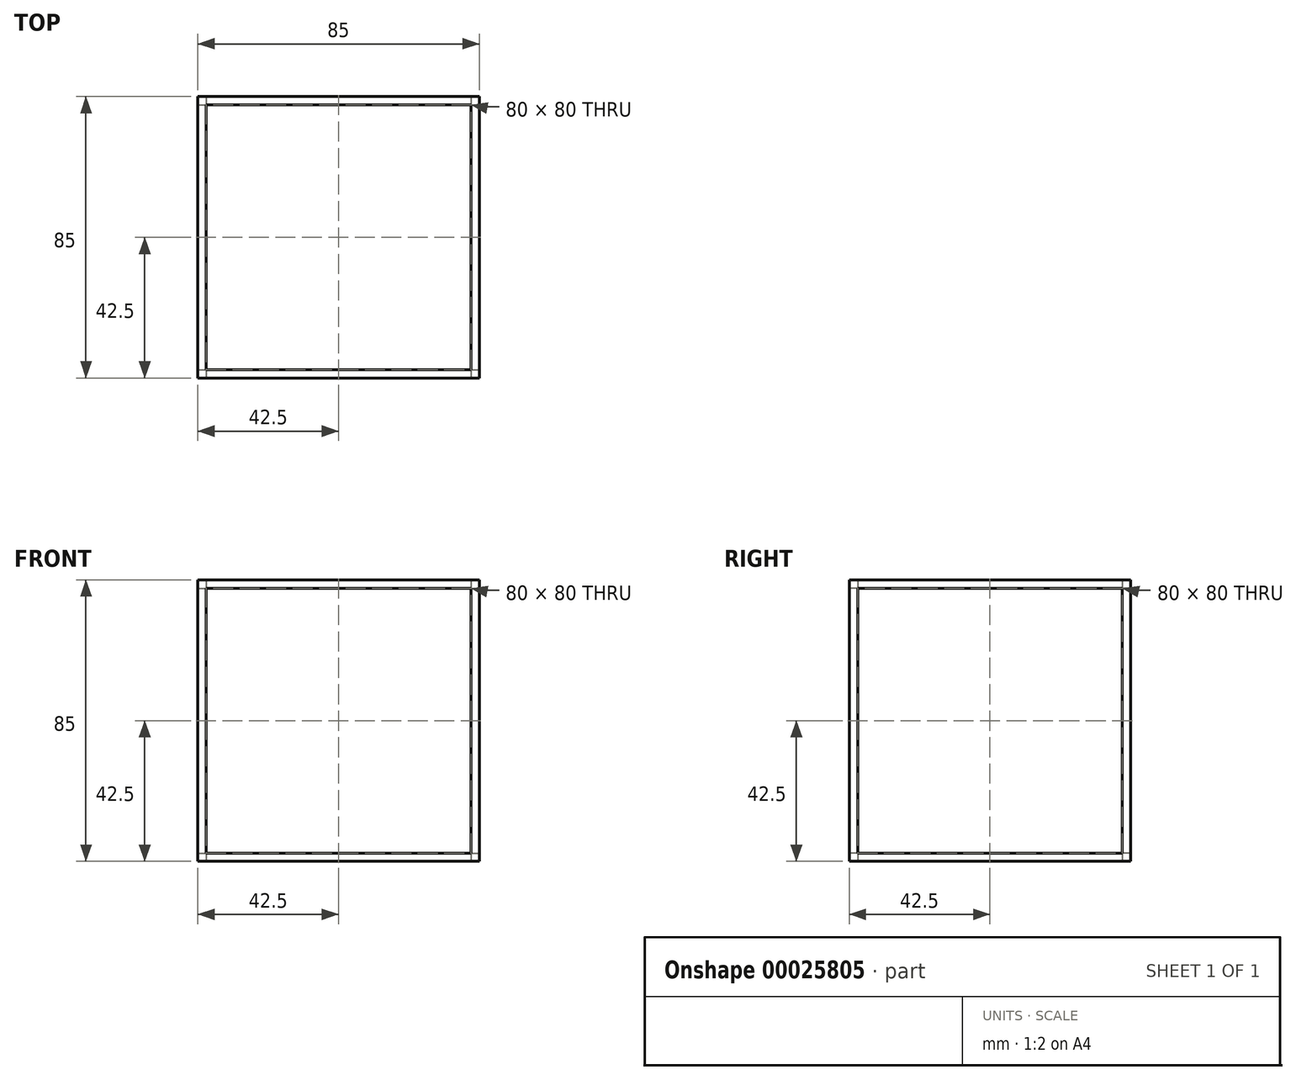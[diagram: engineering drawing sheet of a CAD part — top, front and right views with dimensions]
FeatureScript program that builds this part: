
annotation { "Feature Type Name" : "Feature", "Feature Type Description" : "" }
export const myFeature = defineFeature(function(context is Context, id is Id, definition is map)
    precondition{}
    {
        {
            var Q0;
            Q0=qCreatedBy(makeId("Top.planeOp"),FACE);
            var sketch = newSketch(context, id + "F0", { "sketchPlane" : qUnion([Q0])});
            skLineSegment(sketch, "E0.rect.bottom", {"start": v(-42.5, 42.5) * mm, "end": v(42.5, 42.5) * mm});
            skLineSegment(sketch, "E0.rect.top", {"start": v(-42.5, -42.5) * mm, "end": v(42.5, -42.5) * mm});
            skLineSegment(sketch, "E0.rect.left", {"start": v(-42.5, 42.5) * mm, "end": v(-42.5, -42.5) * mm});
            skLineSegment(sketch, "E0.rect.right", {"start": v(42.5, 42.5) * mm, "end": v(42.5, -42.5) * mm});
            skPoint(sketch, "E0.rect.middle", {"position": v(0, 0) * mm});
            skLineSegment(sketch, "E1.rect.bottom", {"start": v(-40, 40) * mm, "end": v(40, 40) * mm});
            skLineSegment(sketch, "E1.rect.top", {"start": v(-40, -40) * mm, "end": v(40, -40) * mm});
            skLineSegment(sketch, "E1.rect.left", {"start": v(-40, 40) * mm, "end": v(-40, -40) * mm});
            skLineSegment(sketch, "E1.rect.right", {"start": v(40, 40) * mm, "end": v(40, -40) * mm});
            skSolve(sketch);
        }
        {
            var Q0;
            Q0=makeQuery(id+"F0.imprint","IMPRINT",FACE,{"disambiguationData":[TD([[makeQuery(id+"F0.imprint","IMPRINT",EDGE,{"derivedFrom":sQuery(id+"F0.wireOp",EDGE,"E0.rect.bottom")}),-1.0]])]});
            extrude(context, id + "F1", {"entities" : qUnion([Q0]), "depth" : 42.5 * mm, "hasSecondDirection" : true, "secondDirectionOppositeDirection" : true, "secondDirectionDepth" : 42.5 * mm});
        }
        {
            var Q0;
            Q0=qCreatedBy(makeId("Right.planeOp"),FACE);
            var sketch = newSketch(context, id + "F2", { "sketchPlane" : qUnion([Q0])});
            skLineSegment(sketch, "E2.rect.bottom", {"start": v(-42.5, 42.5) * mm, "end": v(42.5, 42.5) * mm});
            skLineSegment(sketch, "E2.rect.top", {"start": v(-42.5, -42.5) * mm, "end": v(42.5, -42.5) * mm});
            skLineSegment(sketch, "E2.rect.left", {"start": v(-42.5, 42.5) * mm, "end": v(-42.5, -42.5) * mm});
            skLineSegment(sketch, "E2.rect.right", {"start": v(42.5, 42.5) * mm, "end": v(42.5, -42.5) * mm});
            skPoint(sketch, "E2.rect.middle", {"position": v(0, 0) * mm});
            skLineSegment(sketch, "E3.rect.bottom", {"start": v(-40, 40) * mm, "end": v(40, 40) * mm});
            skLineSegment(sketch, "E3.rect.top", {"start": v(-40, -40) * mm, "end": v(40, -40) * mm});
            skLineSegment(sketch, "E3.rect.left", {"start": v(-40, 40) * mm, "end": v(-40, -40) * mm});
            skLineSegment(sketch, "E3.rect.right", {"start": v(40, 40) * mm, "end": v(40, -40) * mm});
            skLineSegment(sketch, "E4.top", {"start": v(-40, -36) * mm, "end": v(40, -36) * mm});
            skLineSegment(sketch, "E4.left", {"start": v(-40, -40) * mm, "end": v(-40, -36) * mm});
            skLineSegment(sketch, "E4.right", {"start": v(40, -40) * mm, "end": v(40, -36) * mm});
            skLineSegment(sketch, "E5.bottom", {"start": v(-40, -26) * mm, "end": v(40, -26) * mm});
            skLineSegment(sketch, "E5.top", {"start": v(-40, -35) * mm, "end": v(40, -35) * mm});
            skLineSegment(sketch, "E5.left", {"start": v(-40, -26) * mm, "end": v(-40, -35) * mm});
            skLineSegment(sketch, "E5.right", {"start": v(40, -26) * mm, "end": v(40, -35) * mm});
            skLineSegment(sketch, "E6.bottom", {"start": v(-40, -25) * mm, "end": v(40, -25) * mm});
            skLineSegment(sketch, "E6.top", {"start": v(-40, -16) * mm, "end": v(40, -16) * mm});
            skLineSegment(sketch, "E6.left", {"start": v(-40, -25) * mm, "end": v(-40, -16) * mm});
            skLineSegment(sketch, "E6.right", {"start": v(40, -25) * mm, "end": v(40, -16) * mm});
            skSolve(sketch);
        }
        {
            var Q0;
            Q0=makeQuery(id+"F2.imprint","IMPRINT",FACE,{"disambiguationData":[TD([[makeQuery(id+"F2.imprint","IMPRINT",EDGE,{"derivedFrom":sQuery(id+"F2.wireOp",EDGE,"E2.rect.bottom")}),-1.0]])]});
            extrude(context, id + "F3", {"entities" : qUnion([Q0]), "operationType" : NewBodyOperationType.INTERSECT, "oppositeDirection" : true, "depth" : 42.5 * mm, "hasSecondDirection" : true, "secondDirectionOppositeDirection" : false, "secondDirectionDepth" : 42.5 * mm});
        }
        {
            var Q0;
            Q0=qCreatedBy(makeId("Front.planeOp"),FACE);
            var sketch = newSketch(context, id + "F4", { "sketchPlane" : qUnion([Q0])});
            skLineSegment(sketch, "E7.rect.bottom", {"start": v(-42.5, 42.5) * mm, "end": v(42.5, 42.5) * mm});
            skLineSegment(sketch, "E7.rect.top", {"start": v(-42.5, -42.5) * mm, "end": v(42.5, -42.5) * mm});
            skLineSegment(sketch, "E7.rect.left", {"start": v(-42.5, 42.5) * mm, "end": v(-42.5, -42.5) * mm});
            skLineSegment(sketch, "E7.rect.right", {"start": v(42.5, 42.5) * mm, "end": v(42.5, -42.5) * mm});
            skPoint(sketch, "E7.rect.middle", {"position": v(0, 0) * mm});
            skLineSegment(sketch, "E8.rect.bottom", {"start": v(-40, 40) * mm, "end": v(40, 40) * mm});
            skLineSegment(sketch, "E8.rect.top", {"start": v(-40, -40) * mm, "end": v(40, -40) * mm});
            skLineSegment(sketch, "E8.rect.left", {"start": v(-40, 40) * mm, "end": v(-40, -40) * mm});
            skLineSegment(sketch, "E8.rect.right", {"start": v(40, 40) * mm, "end": v(40, -40) * mm});
            skSolve(sketch);
        }
        {
            var Q0;
            Q0=makeQuery(id+"F4.imprint","IMPRINT",FACE,{"disambiguationData":[TD([[makeQuery(id+"F4.imprint","IMPRINT",EDGE,{"derivedFrom":sQuery(id+"F4.wireOp",EDGE,"E7.rect.bottom")}),-1.0]])]});
            extrude(context, id + "F5", {"entities" : qUnion([Q0]), "operationType" : NewBodyOperationType.INTERSECT, "oppositeDirection" : true, "depth" : 42.5 * mm, "hasSecondDirection" : true, "secondDirectionOppositeDirection" : false, "secondDirectionDepth" : 42.5 * mm});
        }
    });
